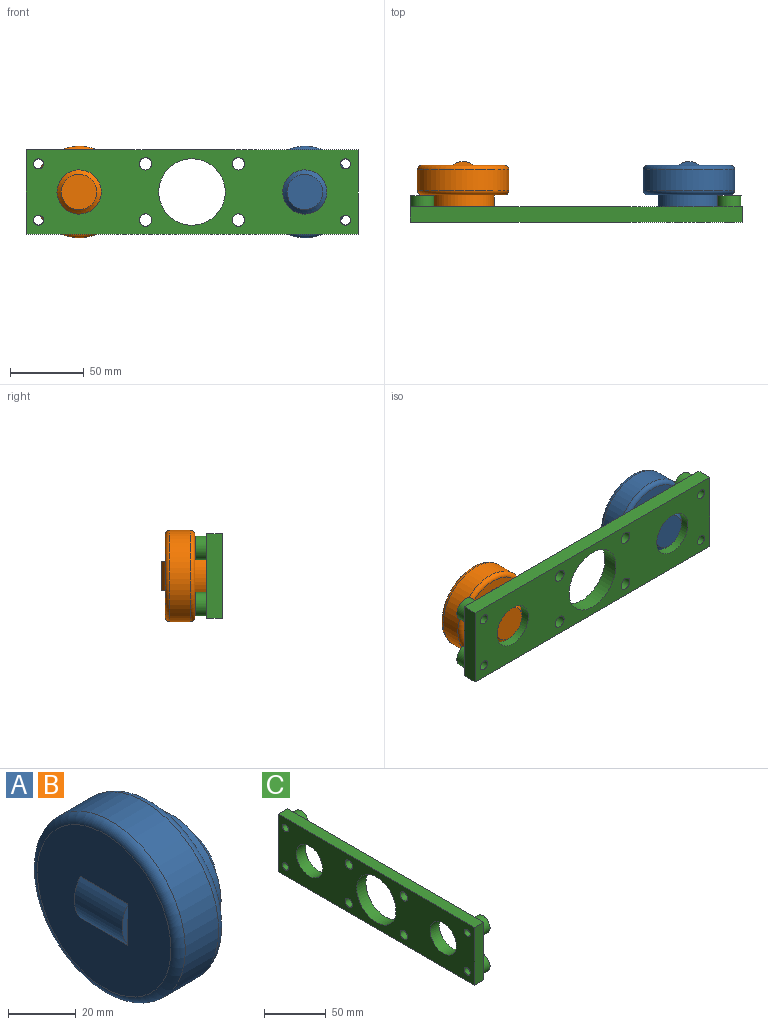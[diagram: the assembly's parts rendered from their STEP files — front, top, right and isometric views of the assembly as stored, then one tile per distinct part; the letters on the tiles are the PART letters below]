
ASSEMBLY  parts=3 mates=1
PART A: 13 faces, bbox 37.5x67.1x67.1 mm
  f0: plane 56x56mm, normal (-1,0,0), area 2163mm2, adj f1,f10,f11,f12
  f1: torus R=28mm, axis (1,0,0), area 885.6mm2, adj f0,f2
  f2: cylinder r=31mm len=62mm, axis (-1,0,0), area 2726.9mm2, adj f1,f3
  f3: torus R=28mm, axis (1,0,0), area 885.6mm2, adj f2,f4
  f4: plane 56x56mm, normal (1,0,0), area 1077.6mm2, adj f3,f5
  f5: cylinder r=21mm len=42mm, axis (-1,0,0), area 1055.6mm2, adj f4,f6
  f6: plane 42x42mm, normal (1,0,0), area 678.6mm2, adj f5,f7
  f7: cylinder r=15mm len=30mm, axis (-1,0,0), area 377mm2, adj f6,f8
  f8: cone r=15mm half-angle=45deg, axis (-1,0,0), area 359.9mm2, adj f7,f9
  f9: plane 24x24mm, normal (1,0,0), area 452.4mm2, adj f8
  f10: cylinder r=12.5mm len=20mm, axis (0,1,0), area 321.8mm2, adj f0,f11,f12
  f11: plane 15x2.5mm, normal (0,-1,0), area 25.5mm2, adj f0,f10
  f12: plane 15x2.5mm, normal (0,1,0), area 25.5mm2, adj f0,f10
PART B: same geometry as A
PART C: 25 faces, bbox 18x225x57.2 mm
  f0: plane 225x10.54mm, normal (0,0,1), area 2371.4mm2, adj f1,f6,f7,f8
  f1: plane 57.15x10.54mm, normal (0,-1,0), area 602.3mm2, adj f0,f2,f7,f8
  f2: plane 225x10.54mm, normal (0,0,-1), area 2371.4mm2, adj f1,f6,f7,f8
  f3: cylinder r=22.5mm len=45mm, axis (-1,0,0), area 1490mm2, adj f7,f8
  f4: cylinder r=15mm len=30mm, axis (-1,0,0), area 993.3mm2, adj f7,f8
  f5: cylinder r=15mm len=30mm, axis (-1,0,0), area 993.3mm2, adj f7,f8
  f6: plane 57.15x10.54mm, normal (0,1,0), area 602.3mm2, adj f0,f2,f7,f8
  f7: plane 225x57.15mm, normal (1,0,0), area 8828.7mm2, adj f0,f1,f2,f3,f4,f5,f6,f9
  f8: plane 225x57.15mm, normal (-1,0,0), area 9487.7mm2, adj f0,f1,f2,f3,f4,f5,f6,f17
  f9: cylinder r=8mm len=16mm, axis (-1,0,0), area 377mm2, adj f7,f10
  f10: plane 16x16mm, normal (1,0,0), area 164.7mm2, adj f9,f24
  f11: cylinder r=8mm len=16mm, axis (-1,0,0), area 377mm2, adj f7,f12
  f12: plane 16x16mm, normal (1,0,0), area 164.7mm2, adj f11,f23
  f13: cylinder r=8mm len=16mm, axis (-1,0,0), area 377mm2, adj f7,f14
  f14: plane 16x16mm, normal (1,0,0), area 164.7mm2, adj f13,f21
  f15: cylinder r=8mm len=16mm, axis (-1,0,0), area 377mm2, adj f7,f16
  f16: plane 16x16mm, normal (1,0,0), area 164.7mm2, adj f15,f22
  f17: cylinder r=4.2mm len=10.54mm, axis (-1,0,0), area 278.1mm2, adj f7,f8
  f18: cylinder r=4.2mm len=10.54mm, axis (-1,0,0), area 278.1mm2, adj f7,f8
  f19: cylinder r=4.2mm len=10.54mm, axis (-1,0,0), area 278.1mm2, adj f7,f8
  f20: cylinder r=4.2mm len=10.54mm, axis (-1,0,0), area 278.1mm2, adj f7,f8
  f21: cylinder r=3.4mm len=18.04mm, axis (-1,0,0), area 385.4mm2, adj f8,f14
  f22: cylinder r=3.4mm len=18.04mm, axis (-1,0,0), area 385.4mm2, adj f8,f16
  f23: cylinder r=3.4mm len=18.04mm, axis (-1,0,0), area 385.4mm2, adj f8,f12
  f24: cylinder r=3.4mm len=18.04mm, axis (-1,0,0), area 385.4mm2, adj f8,f10
PLACE A rot(axis=(0.58,-0.58,-0.58),120deg) t=(386,-449.7,256.5)mm
PLACE B rot(axis=(0.58,-0.58,-0.58),120deg) t=(233,-449.7,256.5)mm
PLACE C rot(axis=(0,0,1),90deg) t=(309.5,-481.3,256.5)mm
MATE fastened C.f4 <-> B.f1  axis (0,1,0) through (233,-474.3,256.5)mm
